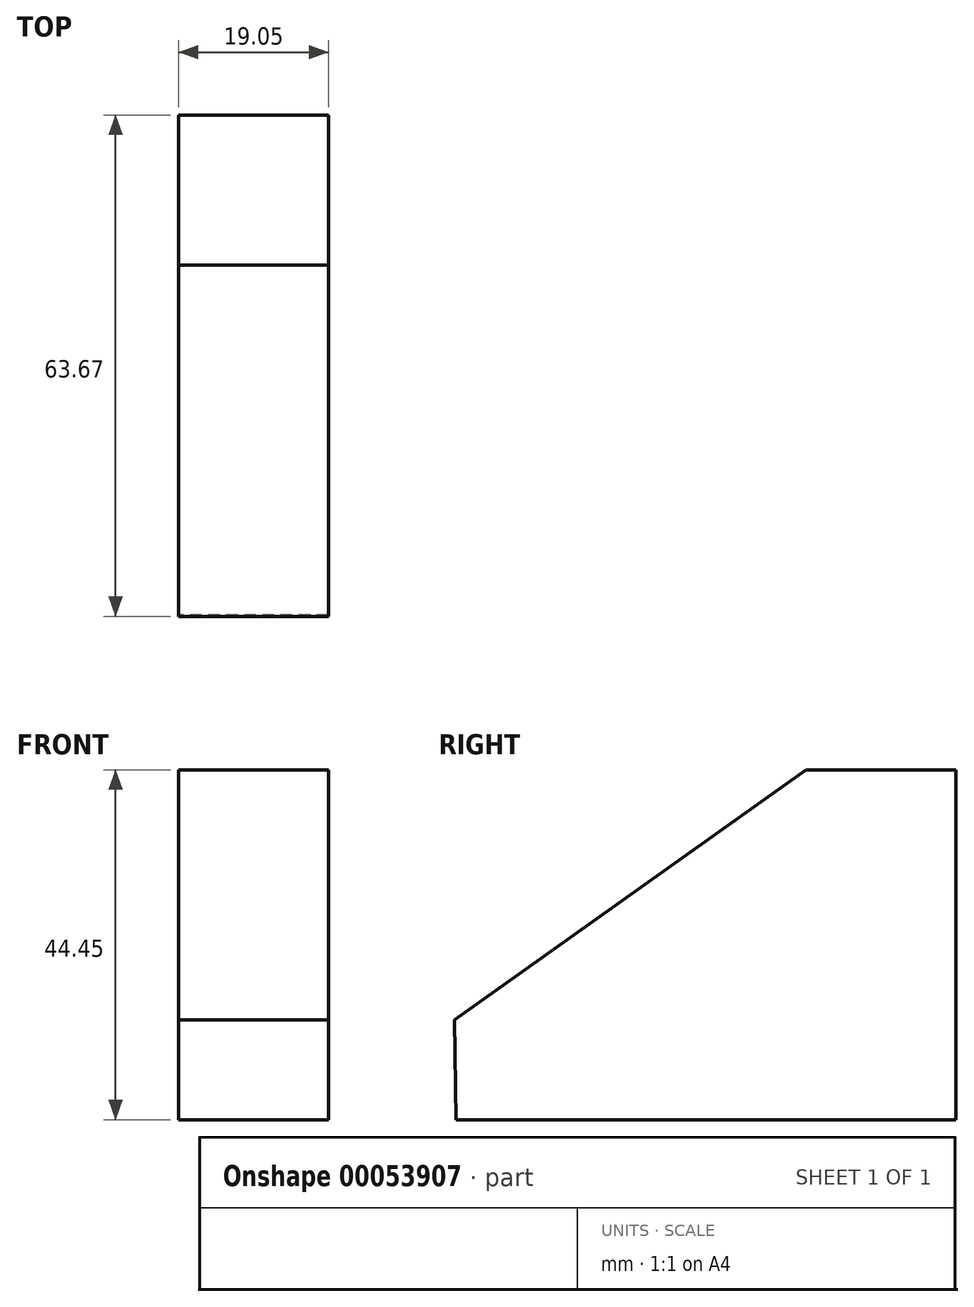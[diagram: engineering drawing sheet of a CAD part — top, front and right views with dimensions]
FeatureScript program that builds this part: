
annotation { "Feature Type Name" : "Feature", "Feature Type Description" : "" }
export const myFeature = defineFeature(function(context is Context, id is Id, definition is map)
    precondition{}
    {
        {
            var Q0;
            Q0=qCreatedBy(makeId("Right.planeOp"),FACE);
            var sketch = newSketch(context, id + "F0", { "sketchPlane" : qUnion([Q0])});
            skLineSegment(sketch, "E0", {"start": v(-71.07, -9.63) * mm, "end": v(-7.57, -9.63) * mm});
            skLineSegment(sketch, "E1", {"start": v(-7.57, -9.63) * mm, "end": v(-7.57, 34.82) * mm});
            skLineSegment(sketch, "E2", {"start": v(-7.57, 34.82) * mm, "end": v(-26.62, 34.82) * mm});
            skLineSegment(sketch, "E3", {"start": v(-26.62, 34.82) * mm, "end": v(-71.24, 3.07) * mm});
            skLineSegment(sketch, "E4", {"start": v(-71.24, 3.07) * mm, "end": v(-71.07, -9.63) * mm});
            skSolve(sketch);
        }
        {
            var Q0;
            Q0 = qSketchRegion(id + "F0", true);
            extrude(context, id + "F1", {"entities" : qUnion([Q0]), "depth" : 19.05 * mm});
        }
    });
